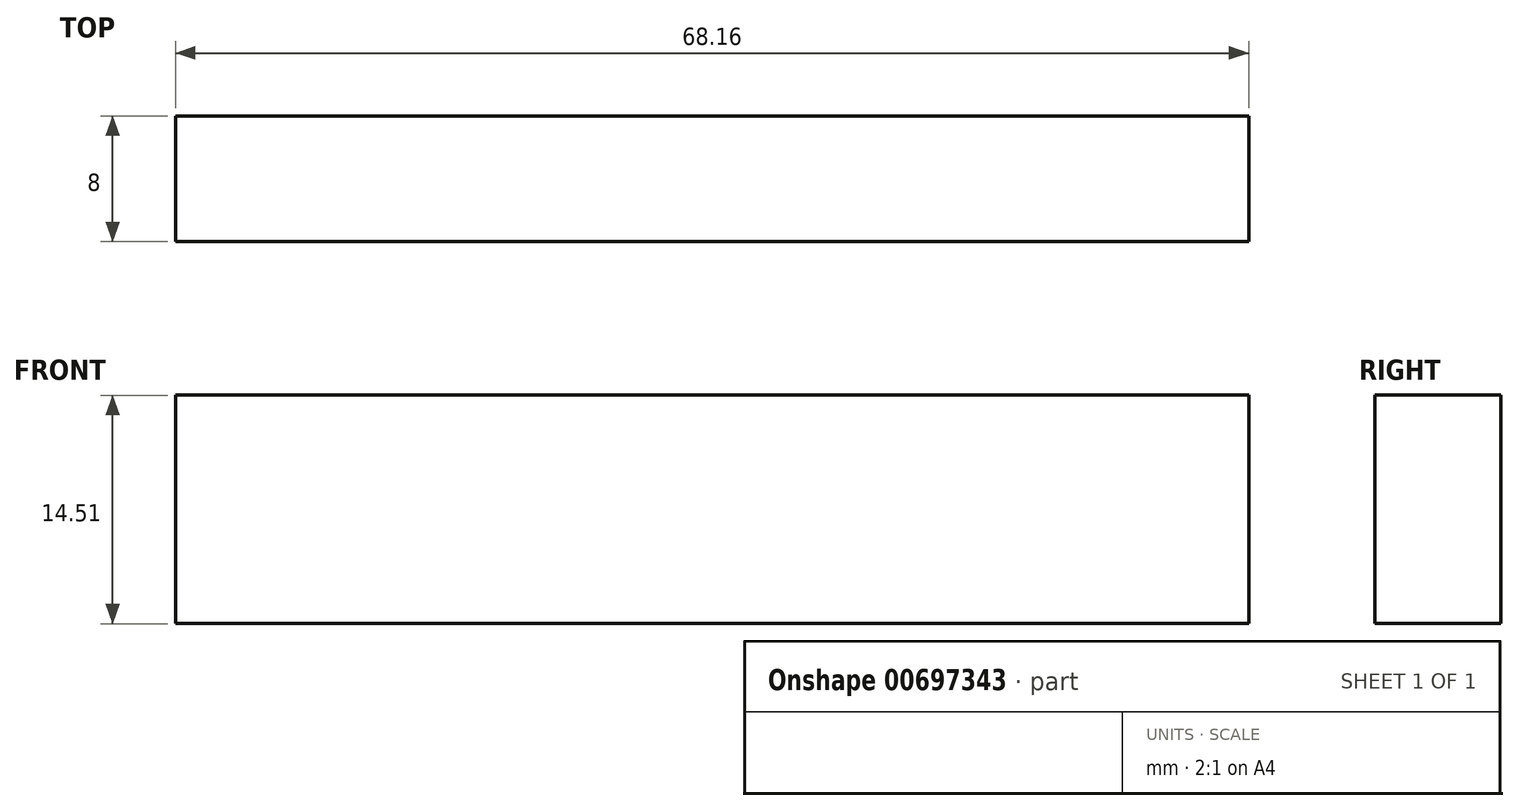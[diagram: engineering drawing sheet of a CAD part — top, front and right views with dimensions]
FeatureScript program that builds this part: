
annotation { "Feature Type Name" : "Feature", "Feature Type Description" : "" }
export const myFeature = defineFeature(function(context is Context, id is Id, definition is map)
    precondition{}
    {
        {
            var Q0;
            Q0=qCreatedBy(makeId("Right.planeOp"),FACE);
            var sketch = newSketch(context, id + "F0", { "sketchPlane" : qUnion([Q0])});
            skLineSegment(sketch, "E0.bottom", {"start": v(8.71, 4.57) * mm, "end": v(-63.24, 4.57) * mm});
            skLineSegment(sketch, "E0.top", {"start": v(8.71, 11.34) * mm, "end": v(-63.24, 11.34) * mm});
            skLineSegment(sketch, "E0.left", {"start": v(8.71, 4.57) * mm, "end": v(8.71, 11.34) * mm});
            skLineSegment(sketch, "E0.right", {"start": v(-63.24, 4.57) * mm, "end": v(-63.24, 11.34) * mm});
            skSolve(sketch);
        }
        {
            var Q0;
            Q0 = qSketchRegion(id + "F0", true);
            extrude(context, id + "F1", {"entities" : qUnion([Q0]), "depth" : 4 * mm, "offsetDistance" : 25 * mm});
        }
        {
            var Q0;
            Q0=makeQuery(id+"F1.opExtrude","SWEPT_BODY",BODY,{"disambiguationData":[OSD([sQuery(id+"F0.wireOp",EDGE,"E0.bottom"),sQuery(id+"F0.wireOp",EDGE,"E0.top"),sQuery(id+"F0.wireOp",EDGE,"E0.left"),sQuery(id+"F0.wireOp",EDGE,"E0.right")])]});
            deleteBodies(context, id + "F2", {"entities" : qUnion([Q0])});
        }
        {
            var Q0;
            Q0=qCreatedBy(makeId("Front.planeOp"),FACE);
            var sketch = newSketch(context, id + "F3", { "sketchPlane" : qUnion([Q0])});
            skLineSegment(sketch, "E1.bottom", {"start": v(-73.38, 49.2) * mm, "end": v(-5.22, 49.2) * mm});
            skLineSegment(sketch, "E1.top", {"start": v(-73.38, 34.7) * mm, "end": v(-5.22, 34.7) * mm});
            skLineSegment(sketch, "E1.left", {"start": v(-73.38, 49.2) * mm, "end": v(-73.38, 34.7) * mm});
            skLineSegment(sketch, "E1.right", {"start": v(-5.22, 49.2) * mm, "end": v(-5.22, 34.7) * mm});
            skSolve(sketch);
        }
        {
            var Q0;
            Q0 = qSketchRegion(id + "F3", true);
            extrude(context, id + "F4", {"entities" : qUnion([Q0]), "depth" : 8 * mm, "offsetDistance" : 25 * mm});
        }
    });
